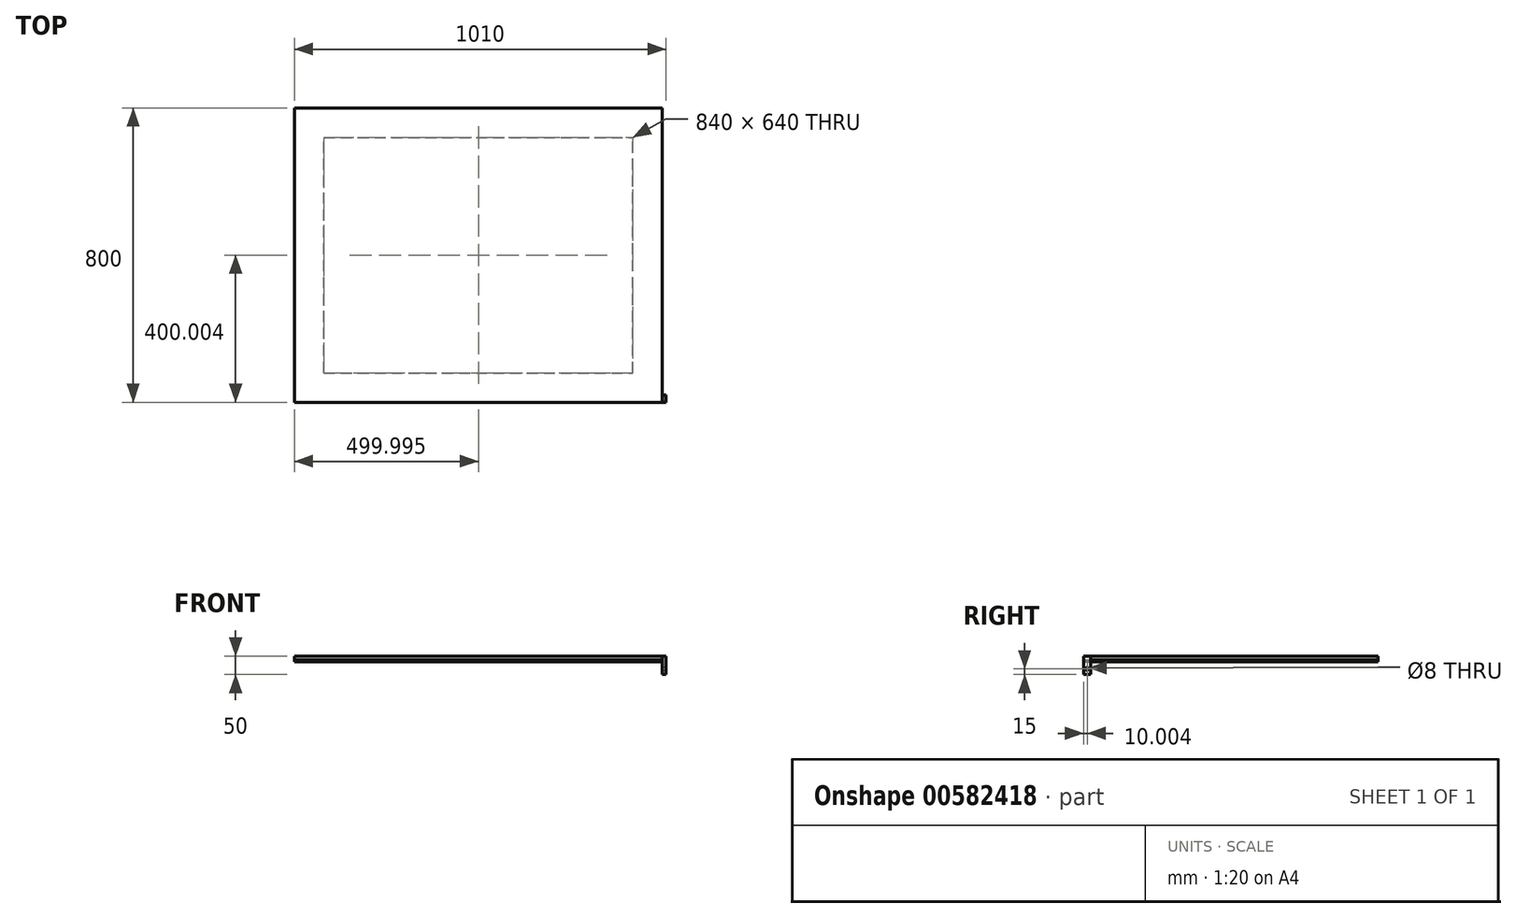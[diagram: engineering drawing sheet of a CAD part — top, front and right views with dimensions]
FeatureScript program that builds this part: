
annotation { "Feature Type Name" : "Feature", "Feature Type Description" : "" }
export const myFeature = defineFeature(function(context is Context, id is Id, definition is map)
    precondition{}
    {
        {
            var Q0;
            Q0=qCreatedBy(makeId("Top.planeOp"),FACE);
            var sketch = newSketch(context, id + "F0", { "sketchPlane" : qUnion([Q0])});
            skLineSegment(sketch, "E0.bottom", {"start": v(-446.06, -309.72) * mm, "end": v(553.94, -309.72) * mm});
            skLineSegment(sketch, "E0.top", {"start": v(-446.06, 490.28) * mm, "end": v(553.94, 490.28) * mm});
            skLineSegment(sketch, "E0.left", {"start": v(-446.06, -309.72) * mm, "end": v(-446.06, 490.28) * mm});
            skLineSegment(sketch, "E0.right", {"start": v(553.94, -309.72) * mm, "end": v(553.94, 490.28) * mm});
            skLineSegment(sketch, "E1.0", {"start": v(-366.06, 410.28) * mm, "end": v(473.94, 410.28) * mm});
            skLineSegment(sketch, "E2.0", {"start": v(-366.06, -309.72) * mm, "end": v(-366.06, 490.28) * mm});
            skLineSegment(sketch, "E3.0", {"start": v(-366.06, -229.72) * mm, "end": v(473.94, -229.72) * mm});
            skLineSegment(sketch, "E4.0", {"start": v(473.94, -309.72) * mm, "end": v(473.94, 490.28) * mm});
            skSolve(sketch);
        }
        {
            var Q0;
            Q0=makeQuery(id+"F0.imprint","IMPRINT",FACE,{"disambiguationData":[TD([[makeQuery(id+"F0.imprint","IMPRINT",EDGE,{"derivedFrom":sQuery(id+"F0.wireOp",EDGE,"E0.bottom")}),1.0]])]});
            var Q1;
            Q1=makeQuery(id+"F0.imprint","IMPRINT",FACE,{"disambiguationData":[TD([[makeQuery(id+"F0.imprint","IMPRINT",EDGE,{"derivedFrom":sQuery(id+"F0.wireOp",EDGE,"DNnGmrQM-lbuE-dcuF-sJEF-m8RkJgQ7nYvQ.bottom")}),1.0]])]});
            var Q2;
            {var subQ4=sQuery(id+"F0.wireOp",EDGE,"E0.left");Q2=makeQuery(id+"F0.imprint","IMPRINT",FACE,{"disambiguationData":[TD([[makeQuery(id+"F0.imprint","IMPRINT",EDGE,{"derivedFrom":subQ4}),-1.0]])]});}
            var Q3;
            {var subQ0=sQuery(id+"F0.wireOp",EDGE,"E1.0");Q3=makeQuery(id+"F0.imprint","IMPRINT",FACE,{"disambiguationData":[TD([[makeQuery(id+"F0.imprint","IMPRINT",EDGE,{"derivedFrom":subQ0}),-1.0]])]});}
            var Q4;
            {var subQ5=sQuery(id+"F0.wireOp",EDGE,"E1.0");Q4=makeQuery(id+"F0.imprint","IMPRINT",FACE,{"disambiguationData":[TD([[makeQuery(id+"F0.imprint","IMPRINT",EDGE,{"derivedFrom":subQ5}),1.0]])]});}
            var Q5;
            {var subQ4=sQuery(id+"F0.wireOp",EDGE,"E0.right");Q5=makeQuery(id+"F0.imprint","IMPRINT",FACE,{"disambiguationData":[TD([[makeQuery(id+"F0.imprint","IMPRINT",EDGE,{"derivedFrom":subQ4}),1.0]])]});}
            extrude(context, id + "F1", {"entities" : qUnion([Q0, Q1, Q2, Q3, Q4, Q5]), "depth" : 10 * mm, "offsetDistance" : 25 * mm});
        }
        {
            var Q0;
            {var subQ4=sQuery(id+"F0.wireOp",EDGE,"E0.left");Q0=makeQuery(id+"F0.imprint","IMPRINT",FACE,{"disambiguationData":[TD([[makeQuery(id+"F0.imprint","IMPRINT",EDGE,{"derivedFrom":subQ4}),-1.0]])]});}
            var Q1;
            {var subQ5=sQuery(id+"F0.wireOp",EDGE,"E1.0");Q1=makeQuery(id+"F0.imprint","IMPRINT",FACE,{"disambiguationData":[TD([[makeQuery(id+"F0.imprint","IMPRINT",EDGE,{"derivedFrom":subQ5}),1.0]])]});}
            var Q2;
            {var subQ5=sQuery(id+"F0.wireOp",EDGE,"E3.0");Q2=makeQuery(id+"F0.imprint","IMPRINT",FACE,{"disambiguationData":[TD([[makeQuery(id+"F0.imprint","IMPRINT",EDGE,{"derivedFrom":subQ5}),-1.0]])]});}
            var Q3;
            {var subQ4=sQuery(id+"F0.wireOp",EDGE,"E0.right");Q3=makeQuery(id+"F0.imprint","IMPRINT",FACE,{"disambiguationData":[TD([[makeQuery(id+"F0.imprint","IMPRINT",EDGE,{"derivedFrom":subQ4}),1.0]])]});}
            extrude(context, id + "F2", {"entities" : qUnion([Q0, Q1, Q2, Q3]), "oppositeDirection" : true, "depth" : 5 * mm, "offsetDistance" : 25 * mm});
        }
        {
            var Q0;
            Q0=makeQuery(id+"F1.opExtrude","SWEPT_FACE",FACE,{"disambiguationData":[OSD([sQuery(id+"F0.wireOp",EDGE,"E0.right")])]});
            var sketch = newSketch(context, id + "F3", { "sketchPlane" : qUnion([Q0])});
            skLineSegment(sketch, "E5.bottom", {"start": v(-309.72, 10) * mm, "end": v(-289.72, 10) * mm});
            skLineSegment(sketch, "E5.top", {"start": v(-309.72, -40) * mm, "end": v(-289.72, -40) * mm});
            skLineSegment(sketch, "E5.left", {"start": v(-309.72, 10) * mm, "end": v(-309.72, -40) * mm});
            skLineSegment(sketch, "E5.right", {"start": v(-289.72, 10) * mm, "end": v(-289.72, -40) * mm});
            skCircle(sketch, "E6", {"center": v(-299.72, -25) * mm, "radius": 4 * mm});
            skPoint(sketch, "E7", {"position": v(-289.72, -5) * mm});
            skSolve(sketch);
        }
        {
            var Q0;
            Q0=qSketchRegion(id+"F3",true);
            extrude(context, id + "F4", {"entities" : qUnion([Q0]), "depth" : 10 * mm, "offsetDistance" : 25 * mm});
        }
    });
